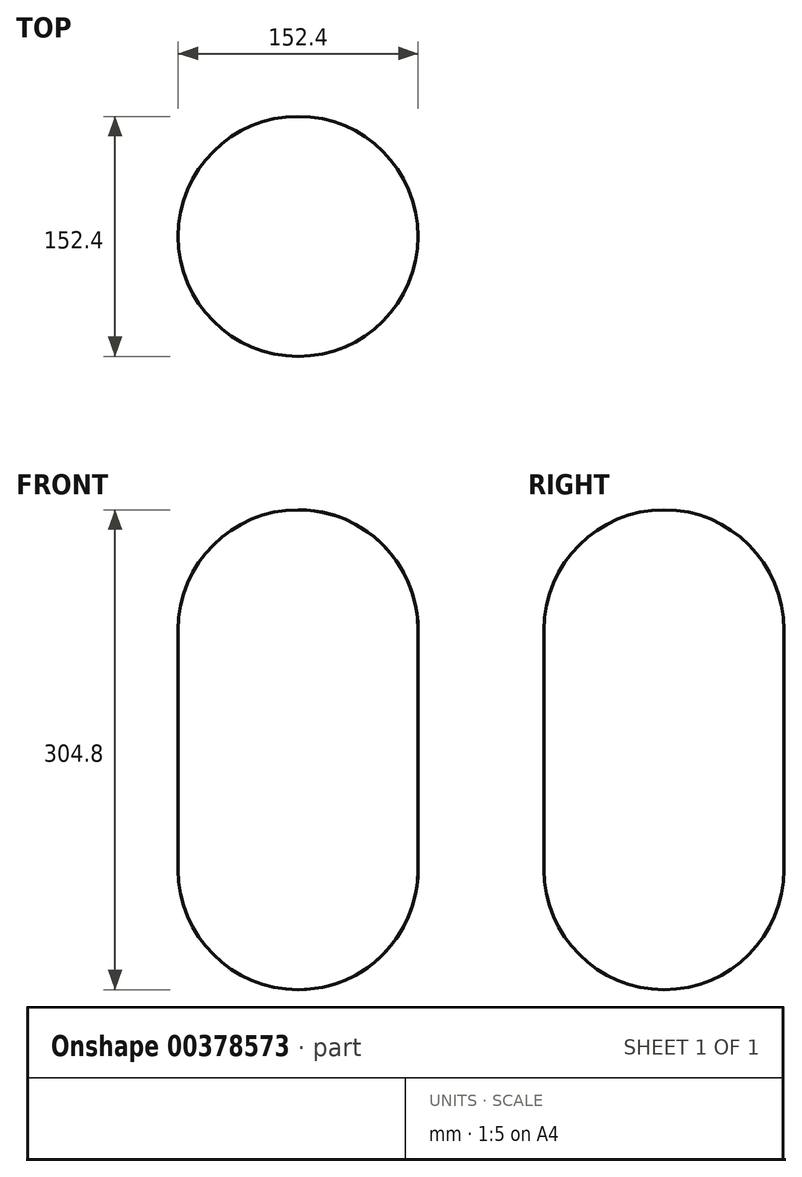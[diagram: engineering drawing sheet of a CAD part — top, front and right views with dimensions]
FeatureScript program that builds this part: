
annotation { "Feature Type Name" : "Feature", "Feature Type Description" : "" }
export const myFeature = defineFeature(function(context is Context, id is Id, definition is map)
    precondition{}
    {
        {
            var Q0;
            Q0=qCreatedBy(makeId("Top.planeOp"),FACE);
            var sketch = newSketch(context, id + "F0", { "sketchPlane" : qUnion([Q0])});
            skCircle(sketch, "E0", {"center": v(0, 0) * mm, "radius": 76.2 * mm});
            skSolve(sketch);
        }
        {
            var Q0;
            Q0 = qSketchRegion(id + "F0", true);
            extrude(context, id + "F1", {"entities" : qUnion([Q0]), "endBound" : BoundingType.SYMMETRIC, "depth" : 304.8 * mm});
        }
        {
            var Q0;
            Q0=makeQuery(id+"F1.opExtrude","SWEPT_FACE",FACE,{"disambiguationData":[OSD([sQuery(id+"F0.wireOp",EDGE,"E0")])]});
            fillet(context, id + "F2", {"entities" : qUnion([Q0]), "radius" : 76.2 * mm, "tangentPropagation" : true, "allowEdgeOverflow" : false});
        }
    });
